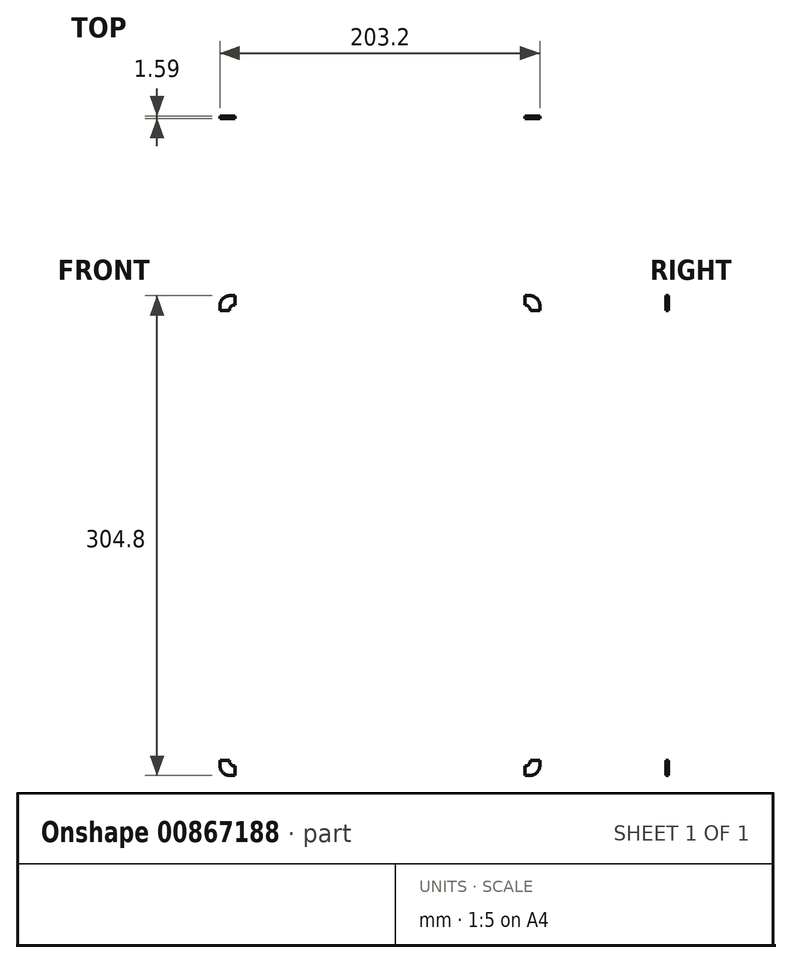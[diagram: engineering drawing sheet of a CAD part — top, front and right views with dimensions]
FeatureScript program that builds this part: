
annotation { "Feature Type Name" : "Feature", "Feature Type Description" : "" }
export const myFeature = defineFeature(function(context is Context, id is Id, definition is map)
    precondition{}
    {
        {
            var Q0;
            Q0=qCreatedBy(makeId("Front.planeOp"),FACE);
            var sketch = newSketch(context, id + "F0", { "sketchPlane" : qUnion([Q0])});
            skLineSegment(sketch, "E0.bottom", {"start": v(-100.35, 262.84) * mm, "end": v(90.15, 262.84) * mm});
            skLineSegment(sketch, "E0.top", {"start": v(-100.35, -41.96) * mm, "end": v(90.15, -41.96) * mm});
            skLineSegment(sketch, "E0.left", {"start": v(-106.7, 256.49) * mm, "end": v(-106.7, -35.61) * mm});
            skLineSegment(sketch, "E0.right", {"start": v(96.5, 256.49) * mm, "end": v(96.5, -35.61) * mm});
            skPoint(sketch, "E1.visualSharp", {"position": v(-106.7, 262.84) * mm});
            skArc(sketch, "E1.filletArc", {"start": v(-100.35, 262.84) * mm, "mid": v(-104.84, 260.98) * mm, "end": v(-106.7, 256.49) * mm});
            skPoint(sketch, "E2.visualSharp", {"position": v(96.5, 262.84) * mm});
            skArc(sketch, "E2.filletArc", {"start": v(96.5, 256.49) * mm, "mid": v(94.64, 260.98) * mm, "end": v(90.15, 262.84) * mm});
            skPoint(sketch, "E3.visualSharp", {"position": v(-106.7, -41.96) * mm});
            skArc(sketch, "E3.filletArc", {"start": v(-106.7, -35.61) * mm, "mid": v(-104.84, -40.1) * mm, "end": v(-100.35, -41.96) * mm});
            skPoint(sketch, "E4.visualSharp", {"position": v(96.5, -41.96) * mm});
            skArc(sketch, "E4.filletArc", {"start": v(90.15, -41.96) * mm, "mid": v(94.64, -40.1) * mm, "end": v(96.5, -35.61) * mm});
            skLineSegment(sketch, "E5.bottom", {"start": v(-106.7, 262.84) * mm, "end": v(-97.17, 262.84) * mm});
            skLineSegment(sketch, "E5.top", {"start": v(-106.7, 253.31) * mm, "end": v(-97.17, 253.31) * mm});
            skLineSegment(sketch, "E5.left", {"start": v(-106.7, 262.84) * mm, "end": v(-106.7, 253.31) * mm});
            skLineSegment(sketch, "E5.right", {"start": v(-97.17, 262.84) * mm, "end": v(-97.17, 253.31) * mm});
            skCircle(sketch, "E6", {"center": v(-97.17, 253.31) * mm, "radius": 3.57 * mm});
            skLineSegment(sketch, "E7.bottom", {"start": v(96.5, 262.84) * mm, "end": v(86.98, 262.84) * mm});
            skLineSegment(sketch, "E7.top", {"start": v(96.5, 253.31) * mm, "end": v(86.98, 253.31) * mm});
            skLineSegment(sketch, "E7.left", {"start": v(96.5, 262.84) * mm, "end": v(96.5, 253.31) * mm});
            skLineSegment(sketch, "E7.right", {"start": v(86.98, 262.84) * mm, "end": v(86.98, 253.31) * mm});
            skCircle(sketch, "E8", {"center": v(86.98, 253.31) * mm, "radius": 3.57 * mm});
            skLineSegment(sketch, "E9.bottom", {"start": v(-106.7, -41.96) * mm, "end": v(-97.17, -41.96) * mm});
            skLineSegment(sketch, "E9.top", {"start": v(-106.7, -32.44) * mm, "end": v(-97.17, -32.44) * mm});
            skLineSegment(sketch, "E9.left", {"start": v(-106.7, -41.96) * mm, "end": v(-106.7, -32.44) * mm});
            skLineSegment(sketch, "E9.right", {"start": v(-97.17, -41.96) * mm, "end": v(-97.17, -32.44) * mm});
            skLineSegment(sketch, "E10.bottom", {"start": v(96.5, -41.96) * mm, "end": v(86.98, -41.96) * mm});
            skLineSegment(sketch, "E10.top", {"start": v(96.5, -32.44) * mm, "end": v(86.98, -32.44) * mm});
            skLineSegment(sketch, "E10.left", {"start": v(96.5, -41.96) * mm, "end": v(96.5, -32.44) * mm});
            skLineSegment(sketch, "E10.right", {"start": v(86.98, -41.96) * mm, "end": v(86.98, -32.44) * mm});
            skCircle(sketch, "E11", {"center": v(-97.17, -32.44) * mm, "radius": 3.57 * mm});
            skCircle(sketch, "E12", {"center": v(86.98, -32.44) * mm, "radius": 3.57 * mm});
            skSolve(sketch);
        }
        {
            var Q0;
            {var subQ3=sQuery(id+"F0.wireOp",EDGE,"E1.filletArc");Q0=makeQuery(id+"F0.imprint","IMPRINT",FACE,{"disambiguationData":[TD([[makeQuery(id+"F0.imprint","IMPRINT",EDGE,{"derivedFrom":subQ3}),1.0]])]});}
            var Q1;
            {var subQ12=sQuery(id+"F0.wireOp",EDGE,"E0.bottom");Q1=makeQuery(id+"F0.imprint","IMPRINT",FACE,{"disambiguationData":[TD([[makeQuery(id+"F0.imprint","IMPRINT",EDGE,{"derivedFrom":subQ12}),-1.0]])]});}
            var Q2;
            {var subQ3=sQuery(id+"F0.wireOp",EDGE,"E2.filletArc");Q2=makeQuery(id+"F0.imprint","IMPRINT",FACE,{"disambiguationData":[TD([[makeQuery(id+"F0.imprint","IMPRINT",EDGE,{"derivedFrom":subQ3}),1.0]])]});}
            var Q3;
            {var subQ3=sQuery(id+"F0.wireOp",EDGE,"E3.filletArc");Q3=makeQuery(id+"F0.imprint","IMPRINT",FACE,{"disambiguationData":[TD([[makeQuery(id+"F0.imprint","IMPRINT",EDGE,{"derivedFrom":subQ3}),1.0]])]});}
            var Q4;
            {var subQ3=sQuery(id+"F0.wireOp",EDGE,"E4.filletArc");Q4=makeQuery(id+"F0.imprint","IMPRINT",FACE,{"disambiguationData":[TD([[makeQuery(id+"F0.imprint","IMPRINT",EDGE,{"derivedFrom":subQ3}),1.0]])]});}
            extrude(context, id + "F1", {"entities" : qUnion([Q0, Q1, Q2, Q3, Q4]), "depth" : 1.59 * mm, "offsetDistance" : 25.4 * mm});
        }
    });
